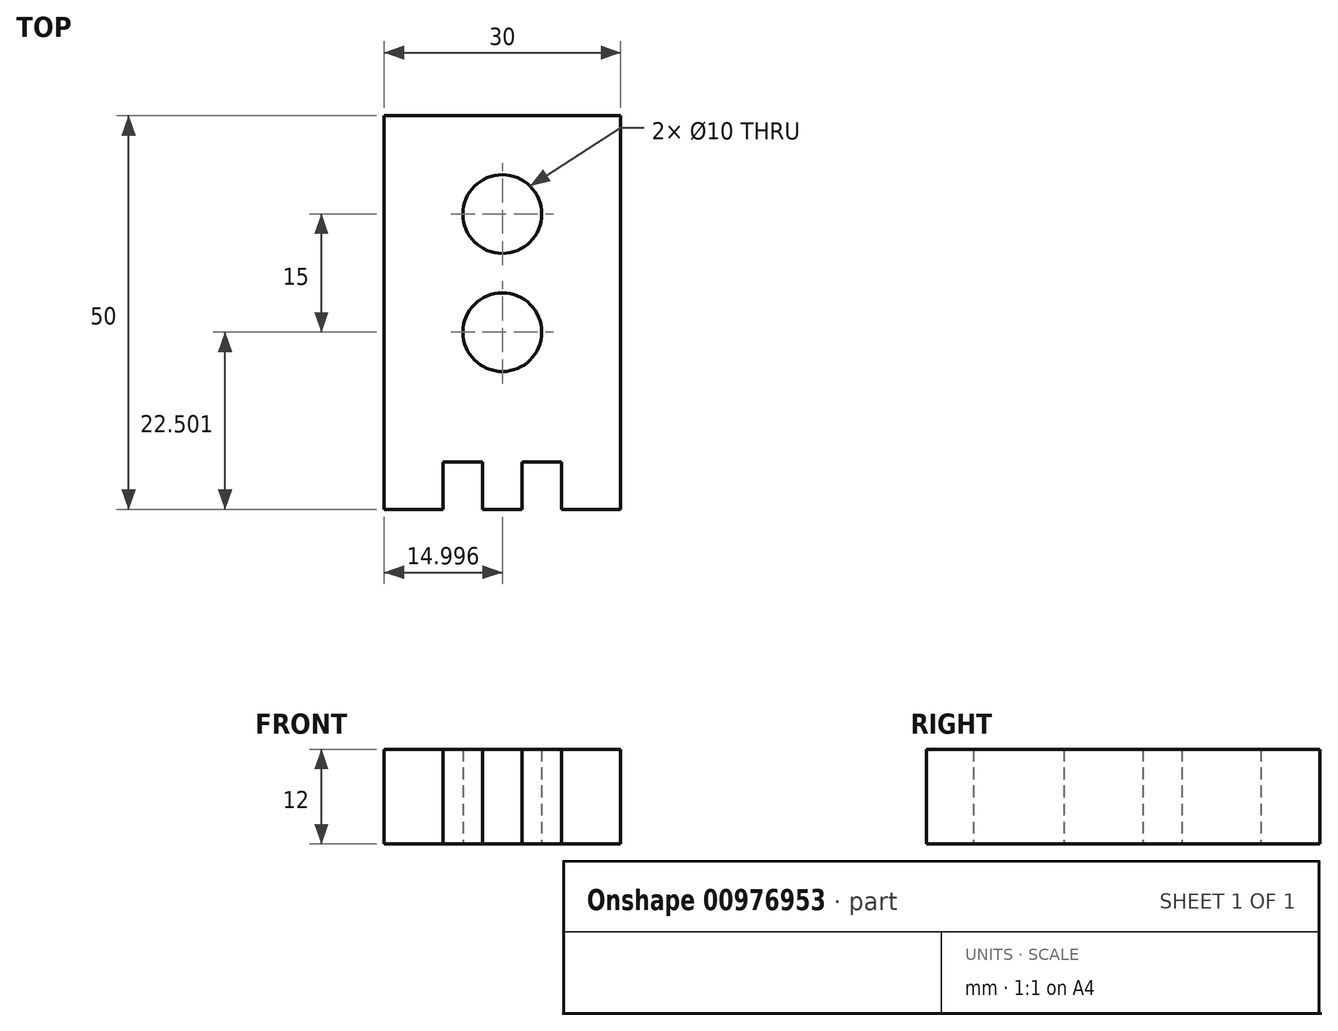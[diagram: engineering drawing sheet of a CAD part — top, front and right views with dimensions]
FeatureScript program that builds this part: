
annotation { "Feature Type Name" : "Feature", "Feature Type Description" : "" }
export const myFeature = defineFeature(function(context is Context, id is Id, definition is map)
    precondition{}
    {
        {
            var Q0;
            Q0=qCreatedBy(makeId("Top.planeOp"),FACE);
            var sketch = newSketch(context, id + "F0", { "sketchPlane" : qUnion([Q0])});
            skLineSegment(sketch, "E0.top", {"start": v(-50.18, 5.87) * mm, "end": v(-20.18, 5.87) * mm});
            skLineSegment(sketch, "E0.left", {"start": v(-50.18, -44.13) * mm, "end": v(-50.18, 5.87) * mm});
            skLineSegment(sketch, "E0.right", {"start": v(-20.18, -44.13) * mm, "end": v(-20.18, 5.87) * mm});
            skLineSegment(sketch, "E1", {"start": v(-42.68, -44.13) * mm, "end": v(-42.68, -38.13) * mm});
            skLineSegment(sketch, "E2", {"start": v(-42.68, -38.13) * mm, "end": v(-37.68, -38.13) * mm});
            skLineSegment(sketch, "E3", {"start": v(-37.68, -38.13) * mm, "end": v(-37.68, -44.13) * mm});
            skLineSegment(sketch, "E4.top", {"start": v(-32.68, -38.13) * mm, "end": v(-27.68, -38.13) * mm});
            skLineSegment(sketch, "E4.left", {"start": v(-32.68, -44.13) * mm, "end": v(-32.68, -38.13) * mm});
            skLineSegment(sketch, "E4.right", {"start": v(-27.68, -44.13) * mm, "end": v(-27.68, -38.13) * mm});
            skLineSegment(sketch, "E5", {"start": v(-50.91, -44.13) * mm, "end": v(-42.68, -44.13) * mm});
            skLineSegment(sketch, "E6", {"start": v(-37.68, -44.13) * mm, "end": v(-32.68, -44.13) * mm});
            skLineSegment(sketch, "E7", {"start": v(-27.68, -44.13) * mm, "end": v(-20.18, -44.13) * mm});
            skSolve(sketch);
        }
        {
            var Q0;
            Q0 = qSketchRegion(id + "F0", true);
            extrude(context, id + "F1", {"entities" : qUnion([Q0]), "depth" : 12 * mm, "offsetDistance" : 25 * mm});
        }
        {
            var Q0;
            Q0=qCreatedBy(makeId("Top.planeOp"),FACE);
            var sketch = newSketch(context, id + "F2", { "sketchPlane" : qUnion([Q0])});
            skCircle(sketch, "E8", {"center": v(-35.18, -6.63) * mm, "radius": 5 * mm});
            skCircle(sketch, "E9", {"center": v(-35.18, -21.63) * mm, "radius": 5 * mm});
            skSolve(sketch);
        }
        {
            var Q0;
            Q0=makeQuery(id+"F2.imprint","IMPRINT",FACE,{"disambiguationData":[TD([[makeQuery(id+"F2.imprint","IMPRINT",EDGE,{"derivedFrom":sQuery(id+"F2.wireOp",EDGE,"E8")}),1.0]])]});
            var Q1;
            Q1=makeQuery(id+"F2.imprint","IMPRINT",FACE,{"disambiguationData":[TD([[makeQuery(id+"F2.imprint","IMPRINT",EDGE,{"derivedFrom":sQuery(id+"F2.wireOp",EDGE,"E9")}),1.0]])]});
            extrude(context, id + "F3", {"entities" : qUnion([Q0, Q1]), "operationType" : NewBodyOperationType.REMOVE, "depth" : 77.7 * mm, "offsetDistance" : 25 * mm});
        }
    });
